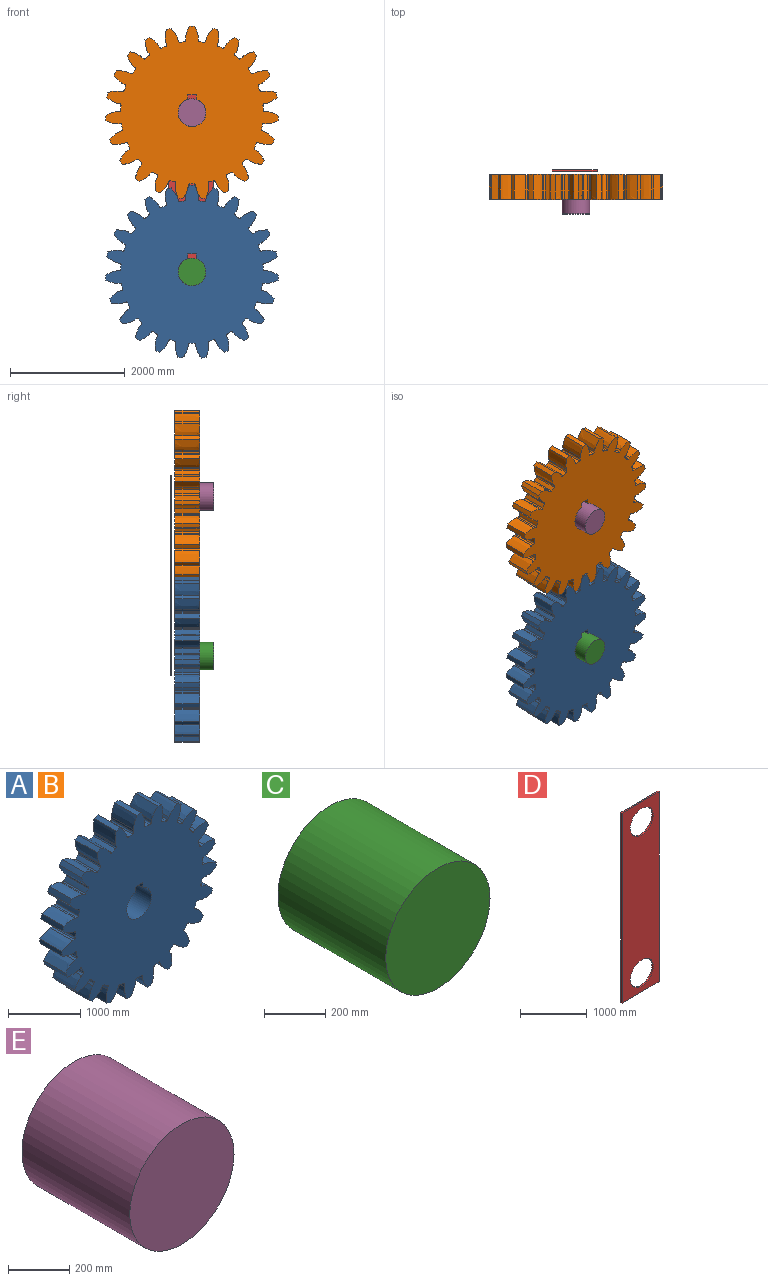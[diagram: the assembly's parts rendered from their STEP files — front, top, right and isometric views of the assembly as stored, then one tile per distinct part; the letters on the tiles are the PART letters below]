
ASSEMBLY  parts=5 mates=6
PART A: 190 faces, bbox 3013.9x431.8x3007.4 mm
  f0: plane 431.8x152.4mm, normal (0,0,-1), area 65806.3mm2, adj f1,f187,f188,f189
  f1: plane 431.8x83.47mm, normal (-1,0,0), area 36041.3mm2, adj f0,f2,f188,f189
  f2: cylinder r=241.3mm len=482.6mm, axis (0,1,0), area 587713.8mm2, adj f1,f187,f188,f189
  f3: extruded ~431.8x207.88mm, area 95144.5mm2, adj f4,f186,f188,f189
  f4: cylinder r=1508.12mm len=431.8mm, axis (0,1,0), area 37025.8mm2, adj f3,f5,f188,f189
  f5: extruded ~431.8x173.58mm, area 95144.5mm2, adj f4,f6,f188,f189
  f6: plane 431.8x31.26mm, normal (0.58,0,0.82), area 16524.3mm2, adj f5,f7,f188,f189
  f7: cylinder r=25.4mm len=431.8mm, axis (0,1,0), area 16069.1mm2, adj f6,f8,f188,f189
  f8: cylinder r=1242.7mm len=431.8mm, axis (0,1,0), area 33182mm2, adj f7,f9,f188,f189
  f9: cylinder r=25.4mm len=431.8mm, axis (0,1,0), area 16069.1mm2, adj f8,f10,f188,f189
  f10: plane 431.8x36.06mm, normal (-0.33,0,-0.94), area 16524.3mm2, adj f9,f11,f188,f189
  f11: extruded ~431.8x218.13mm, area 95144.5mm2, adj f10,f12,f188,f189
  f12: cylinder r=1508.12mm len=431.8mm, axis (0,1,0), area 37025.8mm2, adj f11,f13,f188,f189
  f13: extruded ~431.8x174.27mm, area 95144.5mm2, adj f12,f14,f188,f189
  f14: plane 431.8x36.06mm, normal (0.33,0,0.94), area 16524.3mm2, adj f13,f15,f188,f189
  f15: cylinder r=25.4mm len=431.8mm, axis (0,1,0), area 16069.1mm2, adj f14,f16,f188,f189
  f16: cylinder r=1242.7mm len=431.8mm, axis (0,1,0), area 33182mm2, adj f15,f17,f188,f189
  f17: cylinder r=25.4mm len=431.8mm, axis (0,1,0), area 16069.1mm2, adj f16,f18,f188,f189
  f18: plane 431.8x38.18mm, normal (-0.07,0,-1), area 16524.3mm2, adj f17,f19,f188,f189
  f19: extruded ~431.8x212.21mm, area 95144.5mm2, adj f18,f20,f188,f189
  f20: cylinder r=1508.12mm len=431.8mm, axis (0,1,0), area 37025.8mm2, adj f19,f21,f188,f189
  f21: extruded ~431.8x203.27mm, area 95144.5mm2, adj f20,f22,f188,f189
  f22: plane 431.8x38.18mm, normal (0.07,0,1), area 16524.3mm2, adj f21,f23,f188,f189
  f23: cylinder r=25.4mm len=431.8mm, axis (0,1,0), area 16069.1mm2, adj f22,f24,f188,f189
  f24: cylinder r=1242.7mm len=431.8mm, axis (0,1,0), area 33182mm2, adj f23,f25,f188,f189
  f25: cylinder r=25.4mm len=431.8mm, axis (0,1,0), area 16069.1mm2, adj f24,f26,f188,f189
  f26: plane 431.8x37.47mm, normal (0.2,0,-0.98), area 16524.3mm2, adj f25,f27,f188,f189
  f27: extruded ~431.8x190.55mm, area 95144.5mm2, adj f26,f28,f188,f189
  f28: cylinder r=1508.12mm len=431.8mm, axis (0,1,0), area 37025.8mm2, adj f27,f29,f188,f189
  f29: extruded ~431.8x217.19mm, area 95144.5mm2, adj f28,f30,f188,f189
  f30: plane 431.8x37.47mm, normal (-0.2,0,0.98), area 16524.3mm2, adj f29,f31,f188,f189
  f31: cylinder r=25.4mm len=431.8mm, axis (0,1,0), area 16069.1mm2, adj f30,f32,f188,f189
  f32: cylinder r=1242.7mm len=431.8mm, axis (0,1,0), area 33182mm2, adj f31,f33,f188,f189
  f33: cylinder r=25.4mm len=431.8mm, axis (0,1,0), area 16069.1mm2, adj f32,f34,f188,f189
  f34: plane 431.8x33.98mm, normal (0.46,0,-0.89), area 16524.3mm2, adj f33,f35,f188,f189
  f35: extruded ~431.8x154.75mm, area 95144.5mm2, adj f34,f36,f188,f189
  f36: cylinder r=1508.12mm len=431.8mm, axis (0,1,0), area 37025.8mm2, adj f35,f37,f188,f189
  f37: extruded ~431.8x215.01mm, area 95144.5mm2, adj f36,f38,f188,f189
  f38: plane 431.8x33.98mm, normal (-0.46,0,0.89), area 16524.3mm2, adj f37,f39,f188,f189
  f39: cylinder r=25.4mm len=431.8mm, axis (0,1,0), area 16069.1mm2, adj f38,f40,f188,f189
  f40: cylinder r=1242.7mm len=431.8mm, axis (0,1,0), area 33182mm2, adj f39,f41,f188,f189
  f41: cylinder r=25.4mm len=431.8mm, axis (0,1,0), area 16069.1mm2, adj f40,f42,f188,f189
  f42: plane 431.8x27.97mm, normal (0.68,0,-0.73), area 16524.3mm2, adj f41,f43,f188,f189
  f43: extruded ~431.8x189.98mm, area 95144.5mm2, adj f42,f44,f188,f189
  f44: cylinder r=1508.12mm len=431.8mm, axis (0,1,0), area 37025.8mm2, adj f43,f45,f188,f189
  f45: extruded ~431.8x196.88mm, area 95144.5mm2, adj f44,f46,f188,f189
  f46: plane 431.8x27.97mm, normal (-0.68,0,0.73), area 16524.3mm2, adj f45,f47,f188,f189
  f47: cylinder r=25.4mm len=431.8mm, axis (0,1,0), area 16069.1mm2, adj f46,f48,f188,f189
  f48: cylinder r=1242.7mm len=431.8mm, axis (0,1,0), area 33182mm2, adj f47,f49,f188,f189
  f49: cylinder r=25.4mm len=431.8mm, axis (0,1,0), area 16069.1mm2, adj f48,f50,f188,f189
  f50: plane 431.8x32.7mm, normal (0.85,0,-0.52), area 16524.3mm2, adj f49,f51,f188,f189
  f51: extruded ~431.8x211.94mm, area 95144.5mm2, adj f50,f52,f188,f189
  f52: cylinder r=1508.12mm len=431.8mm, axis (0,1,0), area 37025.8mm2, adj f51,f53,f188,f189
  f53: extruded ~431.8x164.14mm, area 95144.5mm2, adj f52,f54,f188,f189
  f54: plane 431.8x32.7mm, normal (-0.85,0,0.52), area 16524.3mm2, adj f53,f55,f188,f189
  f55: cylinder r=25.4mm len=431.8mm, axis (0,1,0), area 16069.1mm2, adj f54,f56,f188,f189
  f56: cylinder r=1242.7mm len=431.8mm, axis (0,1,0), area 33182mm2, adj f55,f57,f188,f189
  f57: cylinder r=25.4mm len=431.8mm, axis (0,1,0), area 16069.1mm2, adj f56,f58,f188,f189
  f58: plane 431.8x36.85mm, normal (0.96,0,-0.27), area 16524.3mm2, adj f57,f59,f188,f189
  f59: extruded ~431.8x218.17mm, area 95144.5mm2, adj f58,f60,f188,f189
  f60: cylinder r=1508.12mm len=431.8mm, axis (0,1,0), area 37025.8mm2, adj f59,f61,f188,f189
  f61: extruded ~431.8x182.84mm, area 95144.5mm2, adj f60,f62,f188,f189
  f62: plane 431.8x36.85mm, normal (-0.96,0,0.27), area 16524.3mm2, adj f61,f63,f188,f189
  f63: cylinder r=25.4mm len=431.8mm, axis (0,1,0), area 16069.1mm2, adj f62,f64,f188,f189
  f64: cylinder r=1242.7mm len=431.8mm, axis (0,1,0), area 33182mm2, adj f63,f65,f188,f189
  f65: cylinder r=25.4mm len=431.8mm, axis (0,1,0), area 16069.1mm2, adj f64,f66,f188,f189
  f66: plane 431.8x38.27mm, normal (1,0,0), area 16524.3mm2, adj f65,f67,f188,f189
  f67: extruded ~431.8x208.23mm, area 95144.5mm2, adj f66,f68,f188,f189
  f68: cylinder r=1508.12mm len=431.8mm, axis (0,1,0), area 37025.8mm2, adj f67,f69,f188,f189
  f69: extruded ~431.8x208.23mm, area 95144.5mm2, adj f68,f70,f188,f189
  f70: plane 431.8x38.27mm, normal (-1,0,0), area 16524.3mm2, adj f69,f71,f188,f189
  f71: cylinder r=25.4mm len=431.8mm, axis (0,1,0), area 16069.1mm2, adj f70,f72,f188,f189
  f72: cylinder r=1242.7mm len=431.8mm, axis (0,1,0), area 33182mm2, adj f71,f73,f188,f189
  f73: cylinder r=25.4mm len=431.8mm, axis (0,1,0), area 16069.1mm2, adj f72,f74,f188,f189
  f74: plane 431.8x36.85mm, normal (0.96,0,0.27), area 16524.3mm2, adj f73,f75,f188,f189
  f75: extruded ~431.8x182.84mm, area 95144.5mm2, adj f74,f76,f188,f189
  f76: cylinder r=1508.12mm len=431.8mm, axis (0,1,0), area 37025.8mm2, adj f75,f77,f188,f189
  f77: extruded ~431.8x218.17mm, area 95144.5mm2, adj f76,f78,f188,f189
  f78: plane 431.8x36.85mm, normal (-0.96,0,-0.27), area 16524.3mm2, adj f77,f79,f188,f189
  f79: cylinder r=25.4mm len=431.8mm, axis (0,1,0), area 16069.1mm2, adj f78,f80,f188,f189
  f80: cylinder r=1242.7mm len=431.8mm, axis (0,1,0), area 33182mm2, adj f79,f81,f188,f189
  f81: cylinder r=25.4mm len=431.8mm, axis (0,1,0), area 16069.1mm2, adj f80,f82,f188,f189
  f82: plane 431.8x32.7mm, normal (0.85,0,0.52), area 16524.3mm2, adj f81,f83,f188,f189
  f83: extruded ~431.8x164.14mm, area 95144.5mm2, adj f82,f84,f188,f189
  f84: cylinder r=1508.12mm len=431.8mm, axis (0,1,0), area 37025.8mm2, adj f83,f85,f188,f189
  f85: extruded ~431.8x211.94mm, area 95144.5mm2, adj f84,f86,f188,f189
  f86: plane 431.8x32.7mm, normal (-0.85,0,-0.52), area 16524.3mm2, adj f85,f87,f188,f189
  f87: cylinder r=25.4mm len=431.8mm, axis (0,1,0), area 16069.1mm2, adj f86,f88,f188,f189
  f88: cylinder r=1242.7mm len=431.8mm, axis (0,1,0), area 33182mm2, adj f87,f89,f188,f189
  f89: cylinder r=25.4mm len=431.8mm, axis (0,1,0), area 16069.1mm2, adj f88,f90,f188,f189
  f90: plane 431.8x27.97mm, normal (0.68,0,0.73), area 16524.3mm2, adj f89,f91,f188,f189
  f91: extruded ~431.8x196.88mm, area 95144.5mm2, adj f90,f92,f188,f189
  f92: cylinder r=1508.12mm len=431.8mm, axis (0,1,0), area 37025.8mm2, adj f91,f93,f188,f189
  f93: extruded ~431.8x189.98mm, area 95144.5mm2, adj f92,f94,f188,f189
  f94: plane 431.8x27.97mm, normal (-0.68,0,-0.73), area 16524.3mm2, adj f93,f95,f188,f189
  f95: cylinder r=25.4mm len=431.8mm, axis (0,1,0), area 16069.1mm2, adj f94,f96,f188,f189
  f96: cylinder r=1242.7mm len=431.8mm, axis (0,1,0), area 33182mm2, adj f95,f97,f188,f189
  f97: cylinder r=25.4mm len=431.8mm, axis (0,1,0), area 16069.1mm2, adj f96,f98,f188,f189
  f98: plane 431.8x33.98mm, normal (0.46,0,0.89), area 16524.3mm2, adj f97,f99,f188,f189
  f99: extruded ~431.8x215.01mm, area 95144.5mm2, adj f98,f100,f188,f189
  f100: cylinder r=1508.12mm len=431.8mm, axis (0,1,0), area 37025.8mm2, adj f99,f101,f188,f189
  f101: extruded ~431.8x154.75mm, area 95144.5mm2, adj f100,f102,f188,f189
  f102: plane 431.8x33.98mm, normal (-0.46,0,-0.89), area 16524.3mm2, adj f101,f103,f188,f189
  f103: cylinder r=25.4mm len=431.8mm, axis (0,1,0), area 16069.1mm2, adj f102,f104,f188,f189
  f104: cylinder r=1242.7mm len=431.8mm, axis (0,1,0), area 33182mm2, adj f103,f105,f188,f189
  f105: cylinder r=25.4mm len=431.8mm, axis (0,1,0), area 16069.1mm2, adj f104,f106,f188,f189
  f106: plane 431.8x37.47mm, normal (0.2,0,0.98), area 16524.3mm2, adj f105,f107,f188,f189
  f107: extruded ~431.8x217.19mm, area 95144.5mm2, adj f106,f108,f188,f189
  f108: cylinder r=1508.12mm len=431.8mm, axis (0,1,0), area 37025.8mm2, adj f107,f109,f188,f189
  f109: extruded ~431.8x190.55mm, area 95144.5mm2, adj f108,f110,f188,f189
  f110: plane 431.8x37.47mm, normal (-0.2,0,-0.98), area 16524.3mm2, adj f109,f111,f188,f189
  f111: cylinder r=25.4mm len=431.8mm, axis (0,1,0), area 16069.1mm2, adj f110,f112,f188,f189
  f112: cylinder r=1242.7mm len=431.8mm, axis (0,1,0), area 33182mm2, adj f111,f113,f188,f189
  f113: cylinder r=25.4mm len=431.8mm, axis (0,1,0), area 16069.1mm2, adj f112,f114,f188,f189
  f114: plane 431.8x38.18mm, normal (-0.07,0,1), area 16524.3mm2, adj f113,f115,f188,f189
  f115: extruded ~431.8x203.27mm, area 95144.5mm2, adj f114,f116,f188,f189
  f116: cylinder r=1508.12mm len=431.8mm, axis (0,1,0), area 37025.8mm2, adj f115,f117,f188,f189
  f117: extruded ~431.8x212.21mm, area 95144.5mm2, adj f116,f118,f188,f189
  f118: plane 431.8x38.18mm, normal (0.07,0,-1), area 16524.3mm2, adj f117,f119,f188,f189
  f119: cylinder r=25.4mm len=431.8mm, axis (0,1,0), area 16069.1mm2, adj f118,f120,f188,f189
  f120: cylinder r=1242.7mm len=431.8mm, axis (0,1,0), area 33182mm2, adj f119,f121,f188,f189
  f121: cylinder r=25.4mm len=431.8mm, axis (0,1,0), area 16069.1mm2, adj f120,f122,f188,f189
  f122: plane 431.8x36.06mm, normal (-0.33,0,0.94), area 16524.3mm2, adj f121,f123,f188,f189
  f123: extruded ~431.8x174.27mm, area 95144.5mm2, adj f122,f124,f188,f189
  f124: cylinder r=1508.12mm len=431.8mm, axis (0,1,0), area 37025.8mm2, adj f123,f125,f188,f189
  f125: extruded ~431.8x218.13mm, area 95144.5mm2, adj f124,f126,f188,f189
  f126: plane 431.8x36.06mm, normal (0.33,0,-0.94), area 16524.3mm2, adj f125,f127,f188,f189
  f127: cylinder r=25.4mm len=431.8mm, axis (0,1,0), area 16069.1mm2, adj f126,f128,f188,f189
  f128: cylinder r=1242.7mm len=431.8mm, axis (0,1,0), area 33182mm2, adj f127,f129,f188,f189
  f129: cylinder r=25.4mm len=431.8mm, axis (0,1,0), area 16069.1mm2, adj f128,f130,f188,f189
  f130: plane 431.8x31.26mm, normal (-0.58,0,0.82), area 16524.3mm2, adj f129,f131,f188,f189
  f131: extruded ~431.8x173.58mm, area 95144.5mm2, adj f130,f132,f188,f189
  f132: cylinder r=1508.12mm len=431.8mm, axis (0,1,0), area 37025.8mm2, adj f131,f133,f188,f189
  f133: extruded ~431.8x207.88mm, area 95144.5mm2, adj f132,f134,f188,f189
  f134: plane 431.8x31.26mm, normal (0.58,0,-0.82), area 16524.3mm2, adj f133,f135,f188,f189
  f135: cylinder r=25.4mm len=431.8mm, axis (0,1,0), area 16069.1mm2, adj f134,f136,f188,f189
  f136: cylinder r=1242.7mm len=431.8mm, axis (0,1,0), area 33182mm2, adj f135,f137,f188,f189
  f137: cylinder r=25.4mm len=431.8mm, axis (0,1,0), area 16069.1mm2, adj f136,f138,f188,f189
  f138: plane 431.8x29.69mm, normal (-0.78,0,0.63), area 16524.3mm2, adj f137,f139,f188,f189
  f139: extruded ~431.8x202.85mm, area 95144.5mm2, adj f138,f140,f188,f189
  f140: cylinder r=1508.12mm len=431.8mm, axis (0,1,0), area 37025.8mm2, adj f139,f141,f188,f189
  f141: extruded ~431.8x182.21mm, area 95144.5mm2, adj f140,f142,f188,f189
  f142: plane 431.8x29.69mm, normal (0.78,0,-0.63), area 16524.3mm2, adj f141,f143,f188,f189
  f143: cylinder r=25.4mm len=431.8mm, axis (0,1,0), area 16069.1mm2, adj f142,f144,f188,f189
  f144: cylinder r=1242.7mm len=431.8mm, axis (0,1,0), area 33182mm2, adj f143,f145,f188,f189
  f145: cylinder r=25.4mm len=431.8mm, axis (0,1,0), area 16069.1mm2, adj f144,f146,f188,f189
  f146: plane 431.8x35.1mm, normal (-0.92,0,0.4), area 16524.3mm2, adj f145,f147,f188,f189
  f147: extruded ~431.8x217.08mm, area 95144.5mm2, adj f146,f148,f188,f189
  f148: cylinder r=1508.12mm len=431.8mm, axis (0,1,0), area 37025.8mm2, adj f147,f149,f188,f189
  f149: extruded ~431.8x164.9mm, area 95144.5mm2, adj f148,f150,f188,f189
  f150: plane 431.8x35.1mm, normal (0.92,0,-0.4), area 16524.3mm2, adj f149,f151,f188,f189
  f151: cylinder r=25.4mm len=431.8mm, axis (0,1,0), area 16069.1mm2, adj f150,f152,f188,f189
  f152: cylinder r=1242.7mm len=431.8mm, axis (0,1,0), area 33182mm2, adj f151,f153,f188,f189
  f153: cylinder r=25.4mm len=431.8mm, axis (0,1,0), area 16069.1mm2, adj f152,f154,f188,f189
  f154: plane 431.8x37.91mm, normal (-0.99,0,0.14), area 16524.3mm2, adj f153,f155,f188,f189
  f155: extruded ~431.8x215.2mm, area 95144.5mm2, adj f154,f156,f188,f189
  f156: cylinder r=1508.12mm len=431.8mm, axis (0,1,0), area 37025.8mm2, adj f155,f157,f188,f189
  f157: extruded ~431.8x197.37mm, area 95144.5mm2, adj f156,f158,f188,f189
  f158: plane 431.8x37.91mm, normal (0.99,0,-0.14), area 16524.3mm2, adj f157,f159,f188,f189
  f159: cylinder r=25.4mm len=431.8mm, axis (0,1,0), area 16069.1mm2, adj f158,f160,f188,f189
  f160: cylinder r=1242.7mm len=431.8mm, axis (0,1,0), area 33182mm2, adj f159,f161,f188,f189
  f161: cylinder r=25.4mm len=431.8mm, axis (0,1,0), area 16069.1mm2, adj f160,f162,f188,f189
  f162: plane 431.8x37.91mm, normal (-0.99,0,-0.14), area 16524.3mm2, adj f161,f163,f188,f189
  f163: extruded ~431.8x197.37mm, area 95144.5mm2, adj f162,f164,f188,f189
  f164: cylinder r=1508.12mm len=431.8mm, axis (0,1,0), area 37025.8mm2, adj f163,f165,f188,f189
  f165: extruded ~431.8x215.2mm, area 95144.5mm2, adj f164,f166,f188,f189
  f166: plane 431.8x37.91mm, normal (0.99,0,0.14), area 16524.3mm2, adj f165,f167,f188,f189
  f167: cylinder r=25.4mm len=431.8mm, axis (0,1,0), area 16069.1mm2, adj f166,f168,f188,f189
  f168: cylinder r=1242.7mm len=431.8mm, axis (0,1,0), area 33182mm2, adj f167,f169,f188,f189
  f169: cylinder r=25.4mm len=431.8mm, axis (0,1,0), area 16069.1mm2, adj f168,f170,f188,f189
  f170: plane 431.8x35.1mm, normal (-0.92,0,-0.4), area 16524.3mm2, adj f169,f171,f188,f189
  f171: extruded ~431.8x164.9mm, area 95144.5mm2, adj f170,f172,f188,f189
  f172: cylinder r=1508.12mm len=431.8mm, axis (0,1,0), area 37025.8mm2, adj f171,f173,f188,f189
  f173: extruded ~431.8x217.08mm, area 95144.5mm2, adj f172,f174,f188,f189
  f174: plane 431.8x35.1mm, normal (0.92,0,0.4), area 16524.3mm2, adj f173,f175,f188,f189
  f175: cylinder r=25.4mm len=431.8mm, axis (0,1,0), area 16069.1mm2, adj f174,f176,f188,f189
  f176: cylinder r=1242.7mm len=431.8mm, axis (0,1,0), area 33182mm2, adj f175,f177,f188,f189
  f177: cylinder r=25.4mm len=431.8mm, axis (0,1,0), area 16069.1mm2, adj f176,f178,f188,f189
  f178: plane 431.8x29.69mm, normal (-0.78,0,-0.63), area 16524.3mm2, adj f177,f179,f188,f189
  f179: extruded ~431.8x182.21mm, area 95144.5mm2, adj f178,f180,f188,f189
  f180: cylinder r=1508.12mm len=431.8mm, axis (0,1,0), area 37025.8mm2, adj f179,f181,f188,f189
  f181: extruded ~431.8x202.85mm, area 95144.5mm2, adj f180,f182,f188,f189
  f182: plane 431.8x29.69mm, normal (0.78,0,0.63), area 16524.3mm2, adj f181,f183,f188,f189
  f183: cylinder r=25.4mm len=431.8mm, axis (0,1,0), area 16069.1mm2, adj f182,f184,f188,f189
  f184: cylinder r=1242.7mm len=431.8mm, axis (0,1,0), area 33182mm2, adj f183,f185,f188,f189
  f185: cylinder r=25.4mm len=431.8mm, axis (0,1,0), area 16069.1mm2, adj f184,f186,f188,f189
  f186: plane 431.8x31.26mm, normal (-0.58,0,-0.82), area 16524.3mm2, adj f3,f185,f188,f189
  f187: plane 431.8x83.47mm, normal (1,0,0), area 36041.3mm2, adj f0,f2,f188,f189
  f188: plane 3013.85x3007.44mm, normal (0,-1,0), area 5762748.8mm2, adj f0,f1,f2,f3,f4,f5,f6,f7
  f189: plane 3013.85x3007.44mm, normal (0,1,0), area 5762748.9mm2, adj f0,f1,f2,f3,f4,f5,f6,f7
PART B: same geometry as A
PART C: 3 faces, bbox 482.6x500x482.6 mm
  f0: cylinder r=241.3mm len=500mm, axis (0,1,0), area 758066.3mm2, adj f1,f2
  f1: plane 482.6x482.6mm, normal (0,-1,0), area 182921.4mm2, adj f0
  f2: plane 482.6x482.6mm, normal (0,1,0), area 182921.4mm2, adj f0
PART D: 8 faces, bbox 783.3x25x3484.9 mm
  f0: plane 3484.9x25mm, normal (-1,0,0), area 87122.4mm2, adj f1,f5,f6,f7
  f1: plane 783.35x25mm, normal (0,0,-1), area 19583.7mm2, adj f0,f2,f6,f7
  f2: plane 3484.9x25mm, normal (1,0,0), area 87122.4mm2, adj f1,f5,f6,f7
  f3: cylinder r=241.3mm len=482.6mm, axis (0,-1,0), area 37903.3mm2, adj f6,f7
  f4: cylinder r=241.3mm len=482.6mm, axis (0,-1,0), area 37903.3mm2, adj f6,f7
  f5: plane 783.35x25mm, normal (0,0,1), area 19583.7mm2, adj f0,f2,f6,f7
  f6: plane 3484.9x783.35mm, normal (0,1,0), area 2364047.9mm2, adj f0,f1,f2,f3,f4,f5
  f7: plane 3484.9x783.35mm, normal (0,-1,0), area 2364047.9mm2, adj f0,f1,f2,f3,f4,f5
PART E: 3 faces, bbox 482.6x500x482.6 mm
  f0: cylinder r=241.3mm len=500mm, axis (0,1,0), area 758066.3mm2, adj f1,f2
  f1: plane 482.6x482.6mm, normal (0,-1,0), area 182921.4mm2, adj f0
  f2: plane 482.6x482.6mm, normal (0,1,0), area 182921.4mm2, adj f0
PLACE A t=(5110.61,181.8,-1527.6)mm
PLACE B t=(5110.61,181.8,1247.35)mm
PLACE C t=(5110.61,0,-631.93)mm
PLACE D t=(5110.61,237.5,-631.93)mm fixed
PLACE E t=(5110.61,0,-631.93)mm
MATE revolute C.f0 <-> A.f2  axis (0,1,0) through (5110.61,-250,-1532.01)mm
MATE planar B.f188 <-> A.f188  axis (0,-1,0) through (5110.61,-250,1242.4)mm
MATE cylindrical D.f3 <-> C.f0  axis (0,-1,0) through (5110.61,250,-1532.01)mm
MATE revolute E.f0 <-> B.f2  axis (0,1,0) through (5110.61,-250,1242.94)mm
MATE cylindrical D.f4 <-> E.f0  axis (0,-1,0) through (5110.61,250,1242.94)mm
MATE planar E.f0 <-> B.f188  axis (0,-1,0) through (5110.61,-500,1242.94)mm
